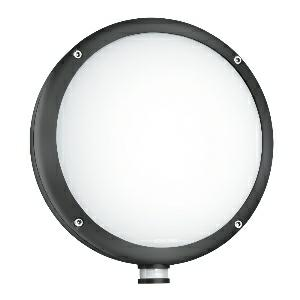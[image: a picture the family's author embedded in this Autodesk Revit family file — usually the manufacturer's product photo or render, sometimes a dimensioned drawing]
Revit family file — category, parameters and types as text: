
# Revit family: l_330_led_053079
name_source: partatom
category: Leuchten
revit_build: Autodesk Revit 2016 (Build: 20190508_0715(x64)
units: mm (PartAtom-declared; Revit-internal decimal feet)

## family parameters
Basisbauteil = Fläche
Beim Laden mit Abzugskörper schneiden = Nein
Bemaßung runder Anschluss = Durchmesser verwenden
Gemeinsam genutzt = Nein
Lichtquelle = Nein
Raumberechnungspunkt = Nein
Teiletyp = Normal

## types (1)
- L 330 LED (1 x , 720 lm, 3000 K)
    Beschreibung = Dimensions (L x W x H): 109 x 253 x 270 mm; Mains power supply: 220 – 240 V / 50 – 60 Hz; Mounting height max.: 2,50 m; Sensor Technology: passive infrared; Output: 9 W; Interconnection: Yes; Type of interconnection: Master/master; Slave modeselectable: No; Luminous flux: 720 lm; Colour temperature: 3000 K; Colour variation LED: SDCM3; Colour Rendering Index CRI: 80-89; With lamp: Yes, STEINEL LED system; Lamp: LED cannot be replaced; LED life expectancy (max. °C): 50000 h; Base: without; LED cooling system: Passive Thermo Control; With motion detector: Yes; Detection angle: 360 °; Sneak-by guard: Yes; Capability of masking out individual segments: Yes; Electronic scalability: No; Mechanical scalability: No; Reach, radial: r = 2 m (13 m²); Reach, tangential: r = 7 m (154 m²); Photo-cell controller: Yes; Twilight setting: 2 – 1000 lx; Time setting: 5 sec – 15 min; Basic light level function: Yes; Basic light level function time: 10/30 min, all night; Functions: 4 programme settings geared to practical needs, can be selected on removable sensor module; Soft light start: Yes; Continuous light: selectable, 4h; Impact resistance: IK10; IP-rating: IP44; Protection class: II; Ambient temperature: -10 – 50 °C; Housing material: Plastic; Cover material: Plastic, opal; Manufacturer's Warranty: 5 years; Settings via: Potentiometers; Cover material: shrouds; Version: Anthracite; PU1, EAN: 4007841053079
    Color Rendering = 80-89
    Color Temperature = 3000 K
    Frequency = 60 Hz, 50 Hz
    Height = 270 mm
    Hersteller = Steinel
    Lamp Light Flux = 720 lm
    Lamp count = 1
    Lampe = 1 x
    Length = 109 mm
    Luminous efficacy = 0 lm/W
    ModVariant = Nein
    Modell = 053079
    Mounting Type = Surface mounted
    Number of Poles = 1
    OnlyDefault = Ja
    Power Factor = 1
    Product Name = L 330 LED
    Product group = Sensor-switched indoor light
    ProductGroupID = 30
    Protection Class = Protection class II
    Protection Degree = IP 34
    RlxData = <blob elided: 42149 chars, md5=04caabf5>
    Scheinlast = 9 VA
    Socket = socket
    Standby Power = 0 W
    System Light Flux = 0 lm
    System Power = 9 W
    Typenbild = produkt1_053079.jpg
    Typenkommentare = Product without accessories
    URL = http://relux.com
    VarID = ---
    Voltage = 0 V
    Vorgabe-Ansicht = 1800 mm
    Weight = 0.00 kg
    Width = 253 mm

## geometry (parser evidence)
native form markers: Sweep x10
no freeform markers — native parametric forms only
